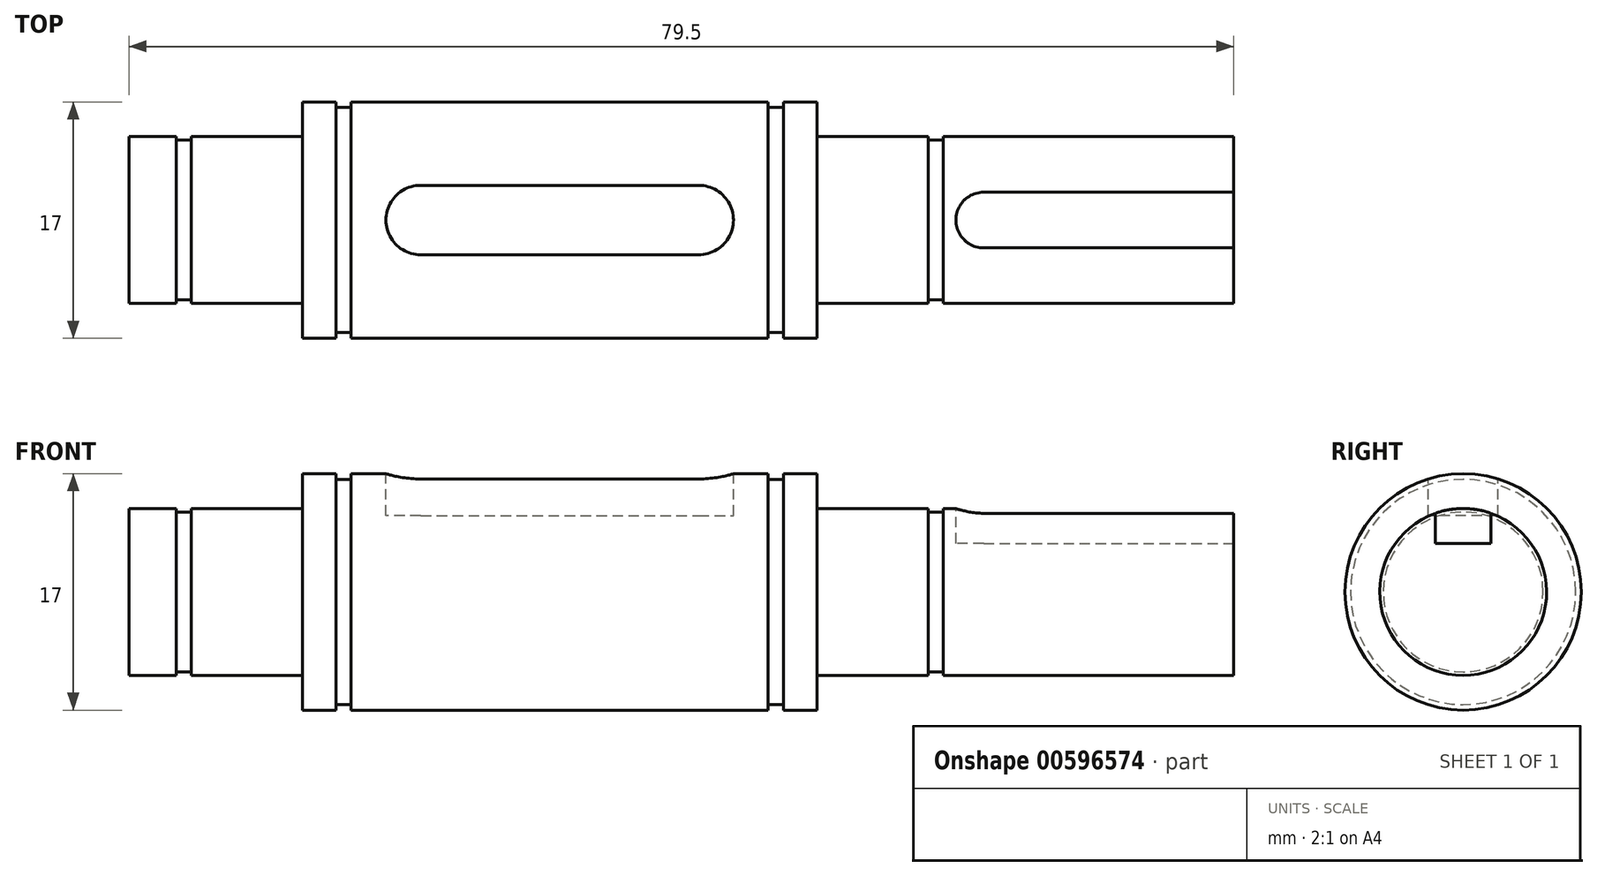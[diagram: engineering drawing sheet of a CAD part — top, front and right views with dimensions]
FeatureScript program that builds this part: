
annotation { "Feature Type Name" : "Feature", "Feature Type Description" : "" }
export const myFeature = defineFeature(function(context is Context, id is Id, definition is map)
    precondition{}
    {
        {
            var Q0;
            Q0=qCreatedBy(makeId("Front.planeOp"),FACE);
            var sketch = newSketch(context, id + "F0", { "sketchPlane" : qUnion([Q0])});
            skLineSegment(sketch, "E0", {"start": v(2.25, 0) * mm, "end": v(64.25, 0) * mm});
            skLineSegment(sketch, "E1", {"start": v(64.25, 6) * mm, "end": v(60.85, 6) * mm});
            skLineSegment(sketch, "E2", {"start": v(51.75, 6) * mm, "end": v(51.75, 8.5) * mm});
            skLineSegment(sketch, "E3", {"start": v(51.75, 8.5) * mm, "end": v(49.35, 8.5) * mm});
            skLineSegment(sketch, "E4", {"start": v(49.35, 8.5) * mm, "end": v(49.35, 8.1) * mm});
            skLineSegment(sketch, "E5", {"start": v(49.35, 8.1) * mm, "end": v(48.25, 8.1) * mm});
            skLineSegment(sketch, "E6", {"start": v(48.25, 8.1) * mm, "end": v(48.25, 8.5) * mm});
            skLineSegment(sketch, "E7", {"start": v(48.25, 8.5) * mm, "end": v(18.25, 8.5) * mm});
            skLineSegment(sketch, "E8", {"start": v(18.25, 8.5) * mm, "end": v(18.25, 8.1) * mm});
            skLineSegment(sketch, "E9", {"start": v(18.25, 8.1) * mm, "end": v(17.15, 8.1) * mm});
            skLineSegment(sketch, "E10", {"start": v(17.15, 8.1) * mm, "end": v(17.15, 8.5) * mm});
            skLineSegment(sketch, "E11", {"start": v(17.15, 8.5) * mm, "end": v(14.75, 8.5) * mm});
            skLineSegment(sketch, "E12", {"start": v(14.75, 8.5) * mm, "end": v(14.75, 6) * mm});
            skLineSegment(sketch, "E13", {"start": v(14.75, 6) * mm, "end": v(6.75, 6) * mm});
            skLineSegment(sketch, "E14", {"start": v(6.75, 6) * mm, "end": v(6.75, 5.75) * mm});
            skLineSegment(sketch, "E15", {"start": v(6.75, 5.75) * mm, "end": v(5.65, 5.75) * mm});
            skLineSegment(sketch, "E16", {"start": v(5.65, 5.75) * mm, "end": v(5.65, 6) * mm});
            skLineSegment(sketch, "E17", {"start": v(5.65, 6) * mm, "end": v(2.25, 6) * mm});
            skLineSegment(sketch, "E18", {"start": v(2.25, 6) * mm, "end": v(2.25, 0) * mm});
            skLineSegment(sketch, "E19", {"start": v(59.75, 5.75) * mm, "end": v(60.85, 5.75) * mm});
            skLineSegment(sketch, "E20", {"start": v(59.75, 5.75) * mm, "end": v(59.75, 6) * mm});
            skLineSegment(sketch, "E21", {"start": v(60.85, 5.75) * mm, "end": v(60.85, 6) * mm});
            skLineSegment(sketch, "E22.trimOffspring", {"start": v(59.75, 6) * mm, "end": v(51.75, 6) * mm});
            skLineSegment(sketch, "E23.0", {"start": v(81.75, 0) * mm, "end": v(81.75, 6) * mm});
            skLineSegment(sketch, "E24", {"start": v(64.25, 6) * mm, "end": v(81.75, 6) * mm});
            skLineSegment(sketch, "E25", {"start": v(64.25, 0) * mm, "end": v(81.75, 0) * mm});
            skSolve(sketch);
        }
        {
            var Q0;
            Q0=makeQuery(id+"F0.imprint","IMPRINT",FACE,{"disambiguationData":[TD([[makeQuery(id+"F0.imprint","IMPRINT",EDGE,{"derivedFrom":sQuery(id+"F0.wireOp",EDGE,"E0")}),1.0]])]});
            var Q1;
            Q1=sQuery(id+"F0.wireOp",EDGE,"E0");
            revolve(context, id + "F1", {"entities" : qUnion([Q0]), "axis" : qUnion([Q1]), "revolveType" : RevolveType.FULL});
        }
        {
            var Q0;
            Q0=qCreatedBy(makeId("Top.planeOp"),FACE);
            cPlane(context, id + "F2", {"entities" : qUnion([Q0]), "cplaneType" : CPlaneType.OFFSET, "offset" : (17 / 2) * mm, "width" : 150 * mm, "height" : 150 * mm});
        }
        {
            var Q0;
            Q0=qCreatedBy(id+"F2.planeOp",FACE);
            var sketch = newSketch(context, id + "F3", { "sketchPlane" : qUnion([Q0])});
            skArc(sketch, "E26", {"start": v(23.25, 2.5) * mm, "mid": v(20.75, 0) * mm, "end": v(23.25, -2.5) * mm});
            skArc(sketch, "E27", {"start": v(43.25, -2.5) * mm, "mid": v(45.75, 0) * mm, "end": v(43.25, 2.5) * mm});
            skLineSegment(sketch, "E28", {"start": v(23.25, 2.5) * mm, "end": v(43.25, 2.5) * mm});
            skLineSegment(sketch, "E29", {"start": v(23.25, -2.5) * mm, "end": v(43.25, -2.5) * mm});
            skSolve(sketch);
        }
        {
            var Q0;
            Q0=makeQuery(id+"F3.imprint","IMPRINT",FACE,{"disambiguationData":[TD([[makeQuery(id+"F3.imprint","IMPRINT",EDGE,{"derivedFrom":sQuery(id+"F3.wireOp",EDGE,"E26")}),1.0]])]});
            extrude(context, id + "F4", {"entities" : qUnion([Q0]), "operationType" : NewBodyOperationType.REMOVE, "oppositeDirection" : true, "depth" : 3 * mm, "offsetDistance" : 25 * mm});
        }
        {
            var Q0;
            Q0=qCreatedBy(makeId("Top.planeOp"),FACE);
            cPlane(context, id + "F5", {"entities" : qUnion([Q0]), "cplaneType" : CPlaneType.OFFSET, "offset" : 6 * mm, "width" : 150 * mm, "height" : 150 * mm});
        }
        {
            var Q0;
            Q0=qCreatedBy(id+"F5.planeOp",FACE);
            var sketch = newSketch(context, id + "F6", { "sketchPlane" : qUnion([Q0])});
            skArc(sketch, "E30", {"start": v(63.75, 2) * mm, "mid": v(61.75, 0) * mm, "end": v(63.75, -2) * mm});
            skLineSegment(sketch, "E31", {"start": v(63.75, 2) * mm, "end": v(82.26, 2) * mm});
            skLineSegment(sketch, "E32", {"start": v(63.75, -2) * mm, "end": v(82.26, -2) * mm});
            skLineSegment(sketch, "E33", {"start": v(82.26, -2) * mm, "end": v(82.26, 2) * mm});
            skPoint(sketch, "E34.orphan", {"position": v(82.54, 2) * mm});
            skSolve(sketch);
        }
        {
            var Q0;
            Q0=makeQuery(id+"F6.imprint","IMPRINT",FACE,{"disambiguationData":[TD([[makeQuery(id+"F6.imprint","IMPRINT",EDGE,{"derivedFrom":sQuery(id+"F6.wireOp",EDGE,"E30")}),1.0]])]});
            extrude(context, id + "F7", {"entities" : qUnion([Q0]), "operationType" : NewBodyOperationType.REMOVE, "oppositeDirection" : true, "depth" : 2.5 * mm, "offsetDistance" : 25 * mm});
        }
    });
